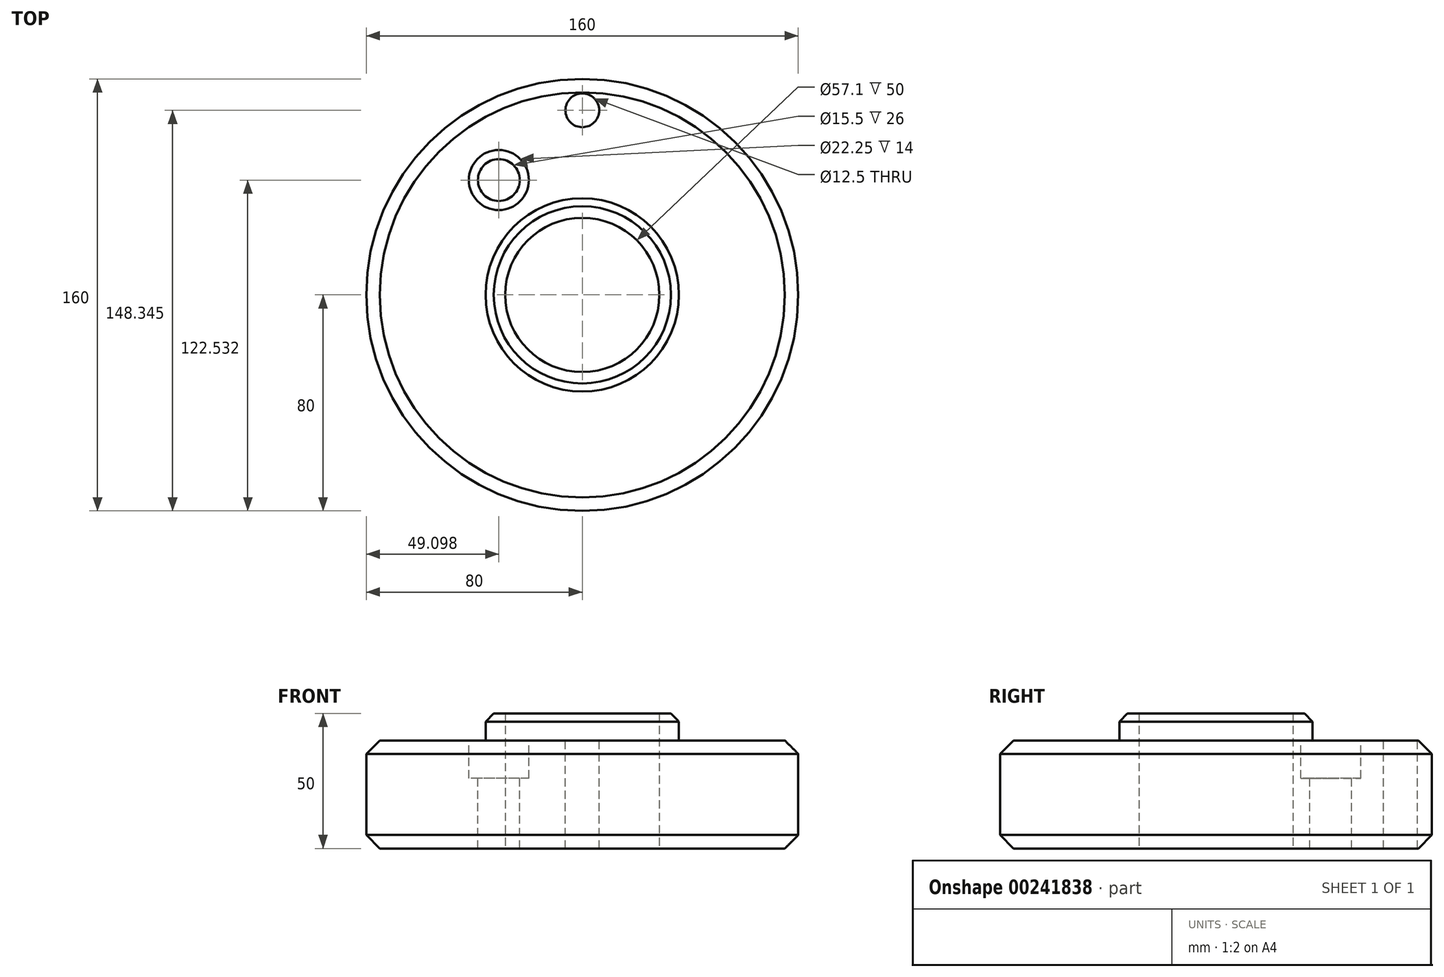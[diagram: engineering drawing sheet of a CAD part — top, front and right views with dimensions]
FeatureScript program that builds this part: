
annotation { "Feature Type Name" : "Feature", "Feature Type Description" : "" }
export const myFeature = defineFeature(function(context is Context, id is Id, definition is map)
    precondition{}
    {
        {
            var Q0;
            Q0=qCreatedBy(makeId("Top.planeOp"),FACE);
            var sketch = newSketch(context, id + "F0", { "sketchPlane" : qUnion([Q0])});
            skCircle(sketch, "E0", {"center": v(0, 0) * mm, "radius": 80 * mm});
            skSolve(sketch);
        }
        {
            var Q0;
            Q0=makeQuery(id+"F0.imprint","IMPRINT",FACE,{"disambiguationData":[TD([[makeQuery(id+"F0.imprint","IMPRINT",EDGE,{"derivedFrom":sQuery(id+"F0.wireOp",EDGE,"E0")}),1.0]])]});
            extrude(context, id + "F1", {"entities" : qUnion([Q0]), "endBound" : BoundingType.SYMMETRIC, "depth" : 40 * mm});
        }
        {
            var Q0;
            Q0=makeQuery(id+"F1.opExtrude","CAP_FACE",FACE,{"disambiguationData":[OSD([sQuery(id+"F0.wireOp",EDGE,"E0")])],"isStart":false});
            var sketch = newSketch(context, id + "F2", { "sketchPlane" : qUnion([Q0])});
            skCircle(sketch, "E1", {"center": v(0, 0) * mm, "radius": 35.8 * mm});
            skSolve(sketch);
        }
        {
            var Q0;
            Q0 = qSketchRegion(id + "F2", true);
            extrude(context, id + "F3", {"entities" : qUnion([Q0]), "operationType" : NewBodyOperationType.ADD, "depth" : 10 * mm});
        }
        {
            var Q0;
            Q0=sQuery(id+"F2.wireOp",EDGE,"E1");
            extrude(context, id + "F4", {"bodyType" : ToolBodyType.SURFACE, "surfaceEntities" : qUnion([Q0]), "oppositeDirection" : true, "depth" : 25.4 * mm});
        }
        {
            var Q0;
            Q0=makeQuery(id+"F1.opExtrude","CAP_FACE",FACE,{"disambiguationData":[OSD([sQuery(id+"F0.wireOp",EDGE,"E0")])],"isStart":true});
            var sketch = newSketch(context, id + "F5", { "sketchPlane" : qUnion([Q0])});
            skSolve(sketch);
        }
        {
            var Q0;
            Q0=makeQuery(id+"F5.imprint","IMPRINT",FACE,{"disambiguationData":[TD([[makeQuery(id+"F5.imprint","IMPRINT",EDGE,{"derivedFrom":makeQuery(id+"F1.opExtrude","CAP_EDGE",EDGE,{"disambiguationData":[OSD([sQuery(id+"F0.wireOp",EDGE,"E0")])],"isStart":true})}),-1.0]])]});
            var sketch = newSketch(context, id + "F6", { "sketchPlane" : qUnion([Q0])});
            skCircle(sketch, "E2", {"center": v(0, 0) * mm, "radius": 28.55 * mm});
            skSolve(sketch);
        }
        {
            var Q0;
            Q0=makeQuery(id+"F6.imprint","IMPRINT",FACE,{"disambiguationData":[TD([[makeQuery(id+"F6.imprint","IMPRINT",EDGE,{"derivedFrom":sQuery(id+"F6.wireOp",EDGE,"E2")}),1.0]])]});
            extrude(context, id + "F7", {"entities" : qUnion([Q0]), "operationType" : NewBodyOperationType.REMOVE, "endBound" : BoundingType.THROUGH_ALL, "oppositeDirection" : true, "depth" : 25.4 * mm});
        }
        {
            var Q0;
            Q0=makeQuery(id+"F1.opExtrude","CAP_FACE",FACE,{"disambiguationData":[OSD([sQuery(id+"F0.wireOp",EDGE,"E0")])],"isStart":false});
            var sketch = newSketch(context, id + "F8", { "sketchPlane" : qUnion([Q0])});
            skCircle(sketch, "E3.cCircle", {"center": v(0, 0) * mm, "radius": 42.53 * mm, "construction": true});
            skLineSegment(sketch, "E3.0", {"start": v(-30.9, 42.53) * mm, "end": v(30.9, 42.53) * mm});
            skLineSegment(sketch, "E3.1", {"start": v(30.9, 42.53) * mm, "end": v(50, -16.25) * mm});
            skLineSegment(sketch, "E3.2", {"start": v(50, -16.25) * mm, "end": v(0, -52.57) * mm});
            skLineSegment(sketch, "E3.3", {"start": v(0, -52.57) * mm, "end": v(-50, -16.25) * mm});
            skLineSegment(sketch, "E3.4", {"start": v(-50, -16.25) * mm, "end": v(-30.9, 42.53) * mm});
            skPoint(sketch, "E3.0.midPoint", {"position": v(0, 42.53) * mm});
            skCircle(sketch, "E4.cCircle", {"center": v(0, 0) * mm, "radius": 55.3 * mm, "construction": true});
            skLineSegment(sketch, "E4.0", {"start": v(0, 68.35) * mm, "end": v(65, 21.12) * mm});
            skLineSegment(sketch, "E4.1", {"start": v(65, 21.12) * mm, "end": v(40.17, -55.3) * mm});
            skLineSegment(sketch, "E4.2", {"start": v(40.17, -55.3) * mm, "end": v(-40.17, -55.3) * mm});
            skLineSegment(sketch, "E4.3", {"start": v(-40.17, -55.3) * mm, "end": v(-65, 21.12) * mm});
            skLineSegment(sketch, "E4.4", {"start": v(-65, 21.12) * mm, "end": v(0, 68.35) * mm});
            skPoint(sketch, "E4.0.midPoint", {"position": v(32.5, 44.73) * mm});
            skSolve(sketch);
        }
        {
            var Q0;
            Q0=sQuery(id+"F8.wireOp",VERTEX,"E3.0.start");
            var Q1;
            Q1=makeQuery(id+"F1.opExtrude","SWEPT_BODY",BODY,{"disambiguationData":[OSD([sQuery(id+"F0.wireOp",EDGE,"E0")])]});
            hole(context, id + "F9", {"style" : HoleStyle.C_BORE, "endStyle" : HoleEndStyle.THROUGH, "standardTappedOrClearance" : lookupTablePath({ "standard" : "ISO", "fit" : "Normal", "size" : "M14", "type" : "Clearance" }), "standardBlindInLast" : lookupTablePath({ "fit" : "Standard", "standard" : "ISO", "size" : "M14", "type" : "Clearance" }), "holeDiameter" : 15.5 * mm, "cBoreDiameter" : 22.25 * mm, "cBoreDepth" : 14 * mm, "locations" : qUnion([Q0]), "scope" : qUnion([Q1]), "isTappedThrough" : true});
        }
        {
            var Q0;
            Q0=sQuery(id+"F8.wireOp",VERTEX,"E4.0.start");
            var Q1;
            Q1=makeQuery(id+"F1.opExtrude","SWEPT_BODY",BODY,{"disambiguationData":[OSD([sQuery(id+"F0.wireOp",EDGE,"E0")])]});
            hole(context, id + "F10", {"style" : HoleStyle.SIMPLE, "endStyle" : HoleEndStyle.THROUGH, "standardTappedOrClearance" : lookupTablePath({ "standard" : "ISO", "engagement" : "75%", "pitch" : "1.5 mm", "size" : "M14", "type" : "Tapped" }), "standardBlindInLast" : lookupTablePath({ "standard" : "ISO", "engagement" : "75%", "pitch" : "1.5 mm", "size" : "M14", "type" : "Tapped" }), "holeDiameter" : 12.5 * mm, "locations" : qUnion([Q0]), "scope" : qUnion([Q1]), "isTappedThrough" : true, "majorDiameter" : 14 * mm, "showTappedDepth" : true});
        }
        {
            var Q0;
            Q0=makeQuery(id+"F1.opExtrude","CAP_EDGE",EDGE,{"disambiguationData":[OSD([sQuery(id+"F0.wireOp",EDGE,"E0")])],"isStart":false});
            var Q1;
            Q1=makeQuery(id+"F7.boolean.opBoolean","COPY",EDGE,{"derivedFrom":makeQuery(id+"F7.opExtrude","CAP_EDGE",EDGE,{"disambiguationData":[OSD([sQuery(id+"F6.wireOp",EDGE,"E2")])],"isStart":true})});
            var Q2;
            Q2=makeQuery(id+"F1.opExtrude","CAP_EDGE",EDGE,{"disambiguationData":[OSD([sQuery(id+"F0.wireOp",EDGE,"E0")])],"isStart":true});
            chamfer(context, id + "F11", {"entities" : qUnion([Q0, Q1, Q2]), "width" : 5 * mm, "tangentPropagation" : true});
        }
        {
            var Q0;
            Q0=makeQuery(id+"F3.opExtrude","CAP_EDGE",EDGE,{"disambiguationData":[OSD([sQuery(id+"F2.wireOp",EDGE,"E1")])],"isStart":false});
            chamfer(context, id + "F12", {"entities" : qUnion([Q0]), "width" : 3 * mm, "tangentPropagation" : true});
        }
    });
